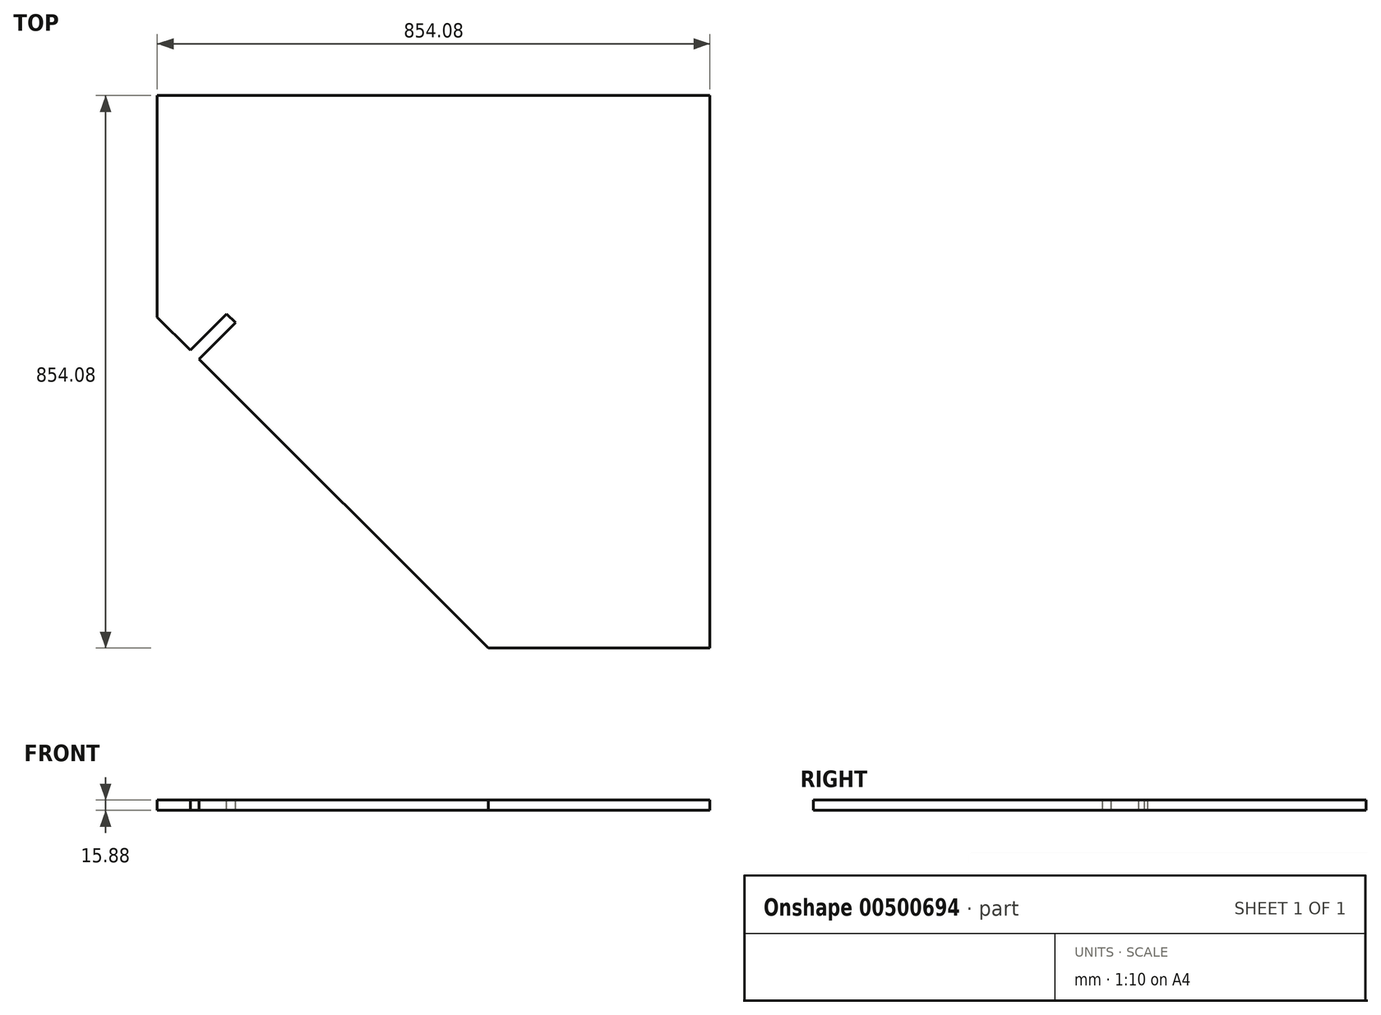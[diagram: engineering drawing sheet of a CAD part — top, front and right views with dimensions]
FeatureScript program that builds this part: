
annotation { "Feature Type Name" : "Feature", "Feature Type Description" : "" }
export const myFeature = defineFeature(function(context is Context, id is Id, definition is map)
    precondition{}
    {
        {
            var Q0;
            Q0=qCreatedBy(makeId("Top.planeOp"),FACE);
            var sketch = newSketch(context, id + "F0", { "sketchPlane" : qUnion([Q0])});
            skLineSegment(sketch, "E0.bottom", {"start": v(488.95, -22.23) * mm, "end": v(854.08, -22.23) * mm});
            skLineSegment(sketch, "E0.top", {"start": v(0, 831.85) * mm, "end": v(854.08, 831.85) * mm});
            skLineSegment(sketch, "E0.left", {"start": v(0, 466.72) * mm, "end": v(0, 831.85) * mm});
            skLineSegment(sketch, "E0.right", {"start": v(854.08, -22.23) * mm, "end": v(854.08, 831.85) * mm});
            skLineSegment(sketch, "E1", {"start": v(488.95, -22.23) * mm, "end": v(0, 466.72) * mm});
            skSolve(sketch);
        }
        {
            var Q0;
            Q0=makeQuery(id+"F0.imprint","IMPRINT",FACE,{"disambiguationData":[TD([[makeQuery(id+"F0.imprint","IMPRINT",EDGE,{"derivedFrom":sQuery(id+"F0.wireOp",EDGE,"E0.bottom")}),1.0]])]});
            extrude(context, id + "F1", {"entities" : qUnion([Q0]), "oppositeDirection" : true, "depth" : 15.88 * mm, "offsetDistance" : 25.4 * mm});
        }
        {
            var Q0;
            Q0=makeQuery(id+"F1.opExtrude","CAP_FACE",FACE,{"disambiguationData":[OSD([sQuery(id+"F0.wireOp",EDGE,"E0.bottom"),sQuery(id+"F0.wireOp",EDGE,"E0.top"),sQuery(id+"F0.wireOp",EDGE,"E0.left"),sQuery(id+"F0.wireOp",EDGE,"E0.right"),sQuery(id+"F0.wireOp",EDGE,"E1")])],"isStart":true});
            var sketch = newSketch(context, id + "F2", { "sketchPlane" : qUnion([Q0])});
            skLineSegment(sketch, "E2", {"start": v(244.48, 222.25) * mm, "end": v(-101.94, 568.66) * mm});
            skLineSegment(sketch, "E3.0", {"start": v(257.29, 231.89) * mm, "end": v(-90.71, 579.89) * mm});
            skLineSegment(sketch, "E4", {"start": v(-101.94, 568.66) * mm, "end": v(-90.71, 579.89) * mm});
            skLineSegment(sketch, "E5", {"start": v(244.48, 222.25) * mm, "end": v(289.08, 266.86) * mm, "construction": true});
            skLineSegment(sketch, "E6.MirrorCS", {"start": v(244.48, 222.25) * mm, "end": v(590.89, -124.16) * mm});
            skLineSegment(sketch, "E7.MirrorCS", {"start": v(254.11, 235.06) * mm, "end": v(602.11, -112.94) * mm});
            skLineSegment(sketch, "E8.MirrorCS", {"start": v(590.89, -124.16) * mm, "end": v(602.11, -112.94) * mm});
            skSolve(sketch);
        }
        {
            var Q0;
            Q0 = qSketchRegion(id + "F2", true);
            extrude(context, id + "F3", {"entities" : qUnion([Q0]), "operationType" : NewBodyOperationType.REMOVE, "oppositeDirection" : true, "depth" : 25.4 * mm, "offsetDistance" : 25.4 * mm});
        }
        {
            var Q0;
            Q0=makeQuery(id+"F1.opExtrude","CAP_FACE",FACE,{"disambiguationData":[OSD([sQuery(id+"F0.wireOp",EDGE,"E0.bottom"),sQuery(id+"F0.wireOp",EDGE,"E0.top"),sQuery(id+"F0.wireOp",EDGE,"E0.left"),sQuery(id+"F0.wireOp",EDGE,"E0.right"),sQuery(id+"F0.wireOp",EDGE,"E1")])],"isStart":true});
            var sketch = newSketch(context, id + "F4", { "sketchPlane" : qUnion([Q0])});
            skLineSegment(sketch, "E9", {"start": v(51.12, 438.05) * mm, "end": v(107.25, 494.18) * mm});
            skLineSegment(sketch, "E10", {"start": v(107.25, 494.18) * mm, "end": v(120.72, 480.7) * mm});
            skLineSegment(sketch, "E11", {"start": v(120.72, 480.7) * mm, "end": v(64.6, 424.58) * mm});
            skLineSegment(sketch, "E12", {"start": v(64.6, 424.58) * mm, "end": v(51.12, 438.05) * mm});
            skSolve(sketch);
        }
        {
            var Q0;
            Q0 = qSketchRegion(id + "F4", true);
            extrude(context, id + "F5", {"entities" : qUnion([Q0]), "operationType" : NewBodyOperationType.REMOVE, "oppositeDirection" : true, "depth" : 25.4 * mm, "offsetDistance" : 25.4 * mm});
        }
    });
